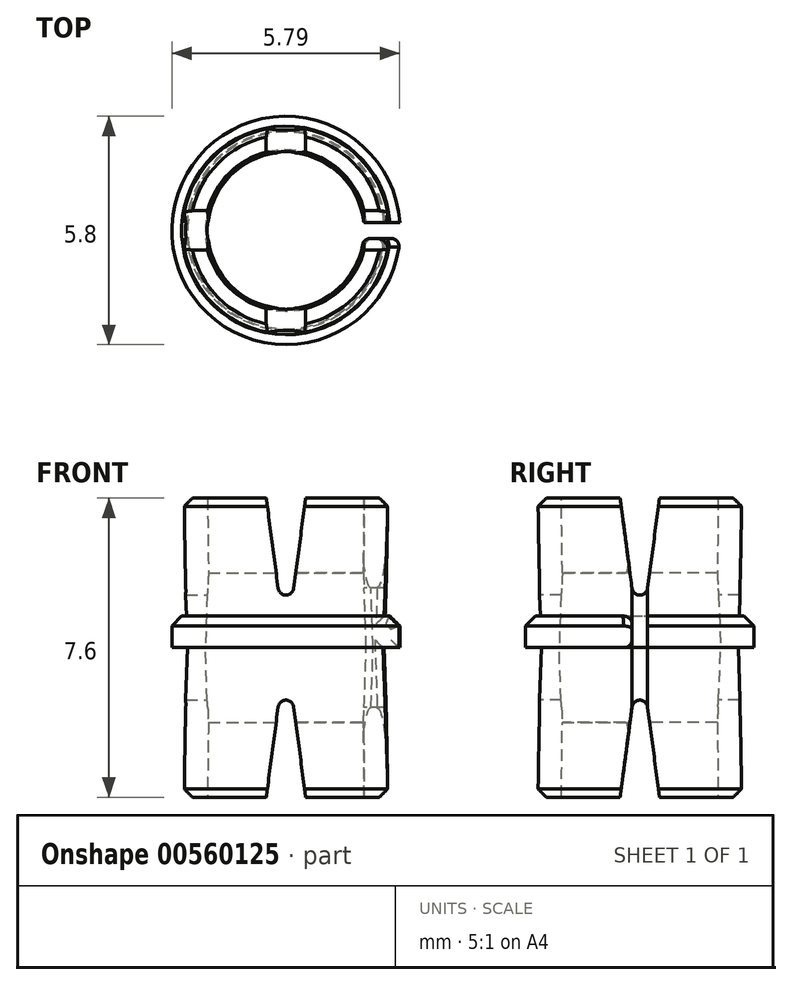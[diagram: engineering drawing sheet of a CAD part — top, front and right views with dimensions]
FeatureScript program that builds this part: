
annotation { "Feature Type Name" : "Feature", "Feature Type Description" : "" }
export const myFeature = defineFeature(function(context is Context, id is Id, definition is map)
    precondition{}
    {
        {
            var Q0;
            Q0=qCreatedBy(makeId("Top.planeOp"),FACE);
            var sketch = newSketch(context, id + "F0", { "sketchPlane" : qUnion([Q0])});
            skCircle(sketch, "E0", {"center": v(0, 0) * mm, "radius": 2.5 * mm});
            skCircle(sketch, "E1", {"center": v(0, 0) * mm, "radius": 2.05 * mm});
            skSolve(sketch);
        }
        {
            var Q0;
            Q0=qSketchRegion(id+"F0",true);
            extrude(context, id + "F1", {"entities" : qUnion([Q0]), "depth" : 3.8 * mm, "offsetDistance" : 25 * mm, "hasDraft" : true, "draftAngle" : 2 * degree, "hasSecondDirection" : true, "secondDirectionOppositeDirection" : true, "secondDirectionDepth" : 3.8 * mm, "hasSecondDirectionDraft" : true, "secondDirectionDraftAngle" : 2 * degree});
        }
        {
            var Q0;
            Q0=qCreatedBy(makeId("Top.planeOp"),FACE);
            var sketch = newSketch(context, id + "F2", { "sketchPlane" : qUnion([Q0])});
            skCircle(sketch, "E2", {"center": v(0, 0) * mm, "radius": 1.92 * mm});
            skSolve(sketch);
        }
        {
            var Q0;
            Q0=qSketchRegion(id+"F2",true);
            extrude(context, id + "F3", {"entities" : qUnion([Q0]), "operationType" : NewBodyOperationType.REMOVE, "endBound" : BoundingType.SYMMETRIC, "oppositeDirection" : true, "depth" : 50 * mm, "offsetDistance" : 25 * mm, "hasDraft" : true, "draftAngle" : 2 * degree});
        }
        {
            var Q0;
            Q0=makeQuery(id+"F1.opExtrude","CAP_EDGE",EDGE,{"disambiguationData":[OSD([sQuery(id+"F0.wireOp",EDGE,"E0")])],"isStart":false});
            var Q1;
            Q1=makeQuery(id+"F1.opExtrude","CAP_EDGE",EDGE,{"disambiguationData":[OSD([sQuery(id+"F0.wireOp",EDGE,"E0")])],"isStart":true});
            chamfer(context, id + "F4", {"entities" : qUnion([Q0, Q1]), "width" : 0.2 * mm, "tangentPropagation" : true});
        }
        {
            var Q0;
            Q0=qCreatedBy(makeId("Right.planeOp"),FACE);
            var sketch = newSketch(context, id + "F5", { "sketchPlane" : qUnion([Q0])});
            skLineSegment(sketch, "E3", {"start": v(0.2, -1.5) * mm, "end": v(0.5, -3.8) * mm});
            skLineSegment(sketch, "E4", {"start": v(0.5, -3.8) * mm, "end": v(-0.5, -3.8) * mm});
            skLineSegment(sketch, "E5", {"start": v(-0.5, -3.8) * mm, "end": v(-0.2, -1.5) * mm});
            skPoint(sketch, "E6.visualSharp", {"position": v(0, 0) * mm});
            skArc(sketch, "E6.filletArc", {"start": v(0.2, -1.5) * mm, "mid": v(0, -1.33) * mm, "end": v(-0.2, -1.5) * mm});
            skArc(sketch, "E7.MirrorCS", {"start": v(0.2, 1.5) * mm, "mid": v(0, 1.33) * mm, "end": v(-0.2, 1.5) * mm});
            skLineSegment(sketch, "E8.MirrorCS", {"start": v(0.2, 1.5) * mm, "end": v(0.5, 3.8) * mm});
            skLineSegment(sketch, "E9.MirrorCS", {"start": v(0.5, 3.8) * mm, "end": v(-0.5, 3.8) * mm});
            skLineSegment(sketch, "E10.MirrorCS", {"start": v(-0.5, 3.8) * mm, "end": v(-0.2, 1.5) * mm});
            skSolve(sketch);
        }
        {
            var Q0;
            Q0=qSketchRegion(id+"F5",true);
            extrude(context, id + "F6", {"entities" : qUnion([Q0]), "operationType" : NewBodyOperationType.REMOVE, "oppositeDirection" : true, "depth" : 25 * mm, "offsetDistance" : 25 * mm, "hasSecondDirection" : true, "secondDirectionOppositeDirection" : false, "secondDirectionDepth" : 25 * mm});
        }
        {
            var Q0;
            Q0=qCreatedBy(makeId("Front.planeOp"),FACE);
            var sketch = newSketch(context, id + "F7", { "sketchPlane" : qUnion([Q0])});
            skLineSegment(sketch, "E11", {"start": v(0.2, -1.5) * mm, "end": v(0.5, -3.8) * mm});
            skLineSegment(sketch, "E12", {"start": v(0.5, -3.8) * mm, "end": v(-0.5, -3.8) * mm});
            skLineSegment(sketch, "E13", {"start": v(-0.5, -3.8) * mm, "end": v(-0.2, -1.5) * mm});
            skPoint(sketch, "E14.visualSharp", {"position": v(0, 0) * mm});
            skArc(sketch, "E14.filletArc", {"start": v(0.2, -1.5) * mm, "mid": v(0, -1.33) * mm, "end": v(-0.2, -1.5) * mm});
            skArc(sketch, "E15.MirrorCS", {"start": v(0.2, 1.5) * mm, "mid": v(0, 1.33) * mm, "end": v(-0.2, 1.5) * mm});
            skLineSegment(sketch, "E16.MirrorCS", {"start": v(0.2, 1.5) * mm, "end": v(0.5, 3.8) * mm});
            skLineSegment(sketch, "E17.MirrorCS", {"start": v(0.5, 3.8) * mm, "end": v(-0.5, 3.8) * mm});
            skLineSegment(sketch, "E18.MirrorCS", {"start": v(-0.5, 3.8) * mm, "end": v(-0.2, 1.5) * mm});
            skSolve(sketch);
        }
        {
            var Q0;
            Q0=qSketchRegion(id+"F7",true);
            extrude(context, id + "F8", {"entities" : qUnion([Q0]), "operationType" : NewBodyOperationType.REMOVE, "oppositeDirection" : true, "depth" : 25 * mm, "offsetDistance" : 25 * mm, "hasSecondDirection" : true, "secondDirectionOppositeDirection" : false, "secondDirectionDepth" : 25 * mm});
        }
        {
            var Q0;
            Q0=qCreatedBy(makeId("Front.planeOp"),FACE);
            var sketch = newSketch(context, id + "F9", { "sketchPlane" : qUnion([Q0])});
            skLineSegment(sketch, "E19.bottom", {"start": v(2.4, 0.8) * mm, "end": v(2.9, 0.8) * mm});
            skLineSegment(sketch, "E19.top", {"start": v(2.4, 0) * mm, "end": v(2.9, 0) * mm});
            skLineSegment(sketch, "E19.left", {"start": v(2.4, 0.8) * mm, "end": v(2.4, 0) * mm});
            skLineSegment(sketch, "E19.right", {"start": v(2.9, 0.8) * mm, "end": v(2.9, 0) * mm});
            skLineSegment(sketch, "E20", {"start": v(0, 0) * mm, "end": v(0, 15.44) * mm, "construction": true});
            skSolve(sketch);
        }
        {
            var Q0;
            Q0=makeQuery(id+"F9.imprint","IMPRINT",FACE,{"disambiguationData":[TD([[makeQuery(id+"F9.imprint","IMPRINT",EDGE,{"derivedFrom":sQuery(id+"F9.wireOp",EDGE,"E19.bottom")}),-1.0]])]});
            var Q1;
            Q1=sQuery(id+"F9.wireOp",EDGE,"E20");
            var Q2;
            Q2=sQuery(id+"F9.wireOp",EDGE,"E20");
            revolve(context, id + "F10", {"operationType" : NewBodyOperationType.ADD, "entities" : qUnion([Q0]), "surfaceEntities" : qUnion([Q1]), "axis" : qUnion([Q2]), "revolveType" : RevolveType.FULL});
        }
        {
            var Q0;
            Q0=makeQuery(id+"F10.opRevolve","SWEPT_EDGE",EDGE,{"disambiguationData":[OSD([sQuery(id+"F9.wireOp",EDGE,"E19.bottom"),sQuery(id+"F9.wireOp",EDGE,"E19.right")])]});
            chamfer(context, id + "F11", {"entities" : qUnion([Q0]), "width" : 0.25 * mm, "tangentPropagation" : true});
        }
        {
            var Q0;
            Q0=qCreatedBy(makeId("Top.planeOp"),FACE);
            var sketch = newSketch(context, id + "F12", { "sketchPlane" : qUnion([Q0])});
            skLineSegment(sketch, "E21", {"start": v(5.06, -0.2) * mm, "end": v(0, -0.2) * mm});
            skLineSegment(sketch, "E22", {"start": v(5.06, 0.2) * mm, "end": v(0, 0.2) * mm});
            skLineSegment(sketch, "E23", {"start": v(0, 0.2) * mm, "end": v(0, -0.2) * mm});
            skLineSegment(sketch, "E24", {"start": v(5.06, 0.2) * mm, "end": v(5.06, -0.2) * mm});
            skSolve(sketch);
        }
        {
            var Q0;
            Q0=makeQuery(id+"F12.imprint","IMPRINT",FACE,{"disambiguationData":[TD([[makeQuery(id+"F12.imprint","IMPRINT",EDGE,{"derivedFrom":sQuery(id+"F12.wireOp",EDGE,"E21")}),-1.0]])]});
            extrude(context, id + "F13", {"entities" : qUnion([Q0]), "operationType" : NewBodyOperationType.REMOVE, "depth" : 25 * mm, "offsetDistance" : 25 * mm, "hasSecondDirection" : true, "secondDirectionOppositeDirection" : true, "secondDirectionDepth" : 25 * mm});
        }
        {
            var Q0;
            Q0=makeQuery(id+"F13.boolean.opBoolean","INTERSECT",EDGE,{"derivedFrom":[makeQuery(id+"F1.*.split.splitOp","SPLIT",FACE,{"derivedFrom":makeQuery(id+"F1.opExtrude","SWEPT_FACE",FACE,{"disambiguationData":[OSD([sQuery(id+"F0.wireOp",EDGE,"E1")])]})}),makeQuery(id+"F13.opExtrude","SWEPT_FACE",FACE,{"disambiguationData":[OSD([sQuery(id+"F12.wireOp",EDGE,"yXu5fMNr-nfGE-pTTA-gAb4-QGezEtGPO8pn")])]})]});
            var Q1;
            Q1=makeQuery(id+"F13.boolean.opBoolean","INTERSECT",EDGE,{"derivedFrom":[makeQuery(id+"F1.*.split.splitOp","SPLIT",FACE,{"derivedFrom":makeQuery(id+"F1.opExtrude","SWEPT_FACE",FACE,{"disambiguationData":[OSD([sQuery(id+"F0.wireOp",EDGE,"E1")])]}),"isFromBackBody":true}),makeQuery(id+"F13.opExtrude","SWEPT_FACE",FACE,{"disambiguationData":[OSD([sQuery(id+"F12.wireOp",EDGE,"yXu5fMNr-nfGE-pTTA-gAb4-QGezEtGPO8pn")])]})]});
            var Q2;
            Q2=makeQuery(id+"F13.boolean.opBoolean","INTERSECT",EDGE,{"derivedFrom":[makeQuery(id+"F1.*.split.splitOp","SPLIT",FACE,{"derivedFrom":makeQuery(id+"F1.opExtrude","SWEPT_FACE",FACE,{"disambiguationData":[OSD([sQuery(id+"F0.wireOp",EDGE,"E1")])]}),"isFromBackBody":true}),makeQuery(id+"F13.opExtrude","SWEPT_FACE",FACE,{"disambiguationData":[OSD([sQuery(id+"F12.wireOp",EDGE,"E21")])]})]});
            var Q3;
            Q3=makeQuery(id+"F13.boolean.opBoolean","INTERSECT",EDGE,{"derivedFrom":[makeQuery(id+"F1.*.split.splitOp","SPLIT",FACE,{"derivedFrom":makeQuery(id+"F1.opExtrude","SWEPT_FACE",FACE,{"disambiguationData":[OSD([sQuery(id+"F0.wireOp",EDGE,"E1")])]})}),makeQuery(id+"F13.opExtrude","SWEPT_FACE",FACE,{"disambiguationData":[OSD([sQuery(id+"F12.wireOp",EDGE,"E21")])]})]});
            var Q4;
            Q4=makeQuery(id+"F13.boolean.opBoolean","INTERSECT",EDGE,{"derivedFrom":[makeQuery(id+"F1.*.split.splitOp","SPLIT",FACE,{"derivedFrom":makeQuery(id+"F1.opExtrude","SWEPT_FACE",FACE,{"disambiguationData":[OSD([sQuery(id+"F0.wireOp",EDGE,"E0")])]}),"isFromBackBody":true}),makeQuery(id+"F13.opExtrude","SWEPT_FACE",FACE,{"disambiguationData":[OSD([sQuery(id+"F12.wireOp",EDGE,"E21")])]})]});
            var Q5;
            Q5=makeQuery(id+"F13.boolean.opBoolean","INTERSECT",EDGE,{"derivedFrom":[makeQuery(id+"F1.*.split.splitOp","SPLIT",FACE,{"derivedFrom":makeQuery(id+"F1.opExtrude","SWEPT_FACE",FACE,{"disambiguationData":[OSD([sQuery(id+"F0.wireOp",EDGE,"E0")])]})}),makeQuery(id+"F13.opExtrude","SWEPT_FACE",FACE,{"disambiguationData":[OSD([sQuery(id+"F12.wireOp",EDGE,"E21")])]})]});
            var Q6;
            Q6=makeQuery(id+"F13.boolean.opBoolean","INTERSECT",EDGE,{"derivedFrom":[makeQuery(id+"F1.*.split.splitOp","SPLIT",FACE,{"derivedFrom":makeQuery(id+"F1.opExtrude","SWEPT_FACE",FACE,{"disambiguationData":[OSD([sQuery(id+"F0.wireOp",EDGE,"E0")])]})}),makeQuery(id+"F13.opExtrude","SWEPT_FACE",FACE,{"disambiguationData":[OSD([sQuery(id+"F12.wireOp",EDGE,"yXu5fMNr-nfGE-pTTA-gAb4-QGezEtGPO8pn")])]})]});
            var Q7;
            Q7=makeQuery(id+"F13.boolean.opBoolean","INTERSECT",EDGE,{"derivedFrom":[makeQuery(id+"F1.*.split.splitOp","SPLIT",FACE,{"derivedFrom":makeQuery(id+"F1.opExtrude","SWEPT_FACE",FACE,{"disambiguationData":[OSD([sQuery(id+"F0.wireOp",EDGE,"E0")])]}),"isFromBackBody":true}),makeQuery(id+"F13.opExtrude","SWEPT_FACE",FACE,{"disambiguationData":[OSD([sQuery(id+"F12.wireOp",EDGE,"yXu5fMNr-nfGE-pTTA-gAb4-QGezEtGPO8pn")])]})]});
            fillet(context, id + "F14", {"entities" : qUnion([Q0, Q1, Q2, Q3, Q4, Q5, Q6, Q7]), "radius" : 0.2 * mm, "tangentPropagation" : true, "allowEdgeOverflow" : false});
        }
        {
            var Q0;
            Q0=makeQuery(id+"F13.boolean.opBoolean","INTERSECT",EDGE,{"derivedFrom":[makeQuery(id+"F10.opRevolve","SWEPT_FACE",FACE,{"disambiguationData":[OSD([sQuery(id+"F9.wireOp",EDGE,"E19.top")])]}),makeQuery(id+"F13.opExtrude","SWEPT_FACE",FACE,{"disambiguationData":[OSD([sQuery(id+"F12.wireOp",EDGE,"E21")])]})]});
            var Q1;
            Q1=makeQuery(id+"F13.boolean.opBoolean","INTERSECT",EDGE,{"derivedFrom":[makeQuery(id+"F10.opRevolve","SWEPT_FACE",FACE,{"disambiguationData":[OSD([sQuery(id+"F9.wireOp",EDGE,"E19.right")])]}),makeQuery(id+"F13.opExtrude","SWEPT_FACE",FACE,{"disambiguationData":[OSD([sQuery(id+"F12.wireOp",EDGE,"E21")])]})]});
            var Q2;
            Q2=makeQuery(id+"F13.boolean.opBoolean","INTERSECT",EDGE,{"derivedFrom":[makeQuery(id+"F11.opChamfer","BLEND_FACE",FACE,{"disambiguationData":[OSD([sQuery(id+"F9.wireOp",EDGE,"E19.bottom"),sQuery(id+"F9.wireOp",EDGE,"E19.right")])]}),makeQuery(id+"F13.opExtrude","SWEPT_FACE",FACE,{"disambiguationData":[OSD([sQuery(id+"F12.wireOp",EDGE,"E21")])]})]});
            var Q3;
            Q3=makeQuery(id+"F13.boolean.opBoolean","INTERSECT",EDGE,{"derivedFrom":[makeQuery(id+"F10.opRevolve","SWEPT_FACE",FACE,{"disambiguationData":[OSD([sQuery(id+"F9.wireOp",EDGE,"E19.bottom")])]}),makeQuery(id+"F13.opExtrude","SWEPT_FACE",FACE,{"disambiguationData":[OSD([sQuery(id+"F12.wireOp",EDGE,"E21")])]})]});
            var Q4;
            Q4=makeQuery(id+"F13.boolean.opBoolean","INTERSECT",EDGE,{"derivedFrom":[makeQuery(id+"F10.opRevolve","SWEPT_FACE",FACE,{"disambiguationData":[OSD([sQuery(id+"F9.wireOp",EDGE,"E19.top")])]}),makeQuery(id+"F13.opExtrude","SWEPT_FACE",FACE,{"disambiguationData":[OSD([sQuery(id+"F12.wireOp",EDGE,"yXu5fMNr-nfGE-pTTA-gAb4-QGezEtGPO8pn")])]})]});
            var Q5;
            Q5=makeQuery(id+"F13.boolean.opBoolean","INTERSECT",EDGE,{"derivedFrom":[makeQuery(id+"F10.opRevolve","SWEPT_FACE",FACE,{"disambiguationData":[OSD([sQuery(id+"F9.wireOp",EDGE,"E19.right")])]}),makeQuery(id+"F13.opExtrude","SWEPT_FACE",FACE,{"disambiguationData":[OSD([sQuery(id+"F12.wireOp",EDGE,"yXu5fMNr-nfGE-pTTA-gAb4-QGezEtGPO8pn")])]})]});
            var Q6;
            Q6=makeQuery(id+"F13.boolean.opBoolean","INTERSECT",EDGE,{"derivedFrom":[makeQuery(id+"F11.opChamfer","BLEND_FACE",FACE,{"disambiguationData":[OSD([sQuery(id+"F9.wireOp",EDGE,"E19.bottom"),sQuery(id+"F9.wireOp",EDGE,"E19.right")])]}),makeQuery(id+"F13.opExtrude","SWEPT_FACE",FACE,{"disambiguationData":[OSD([sQuery(id+"F12.wireOp",EDGE,"yXu5fMNr-nfGE-pTTA-gAb4-QGezEtGPO8pn")])]})]});
            var Q7;
            Q7=makeQuery(id+"F13.boolean.opBoolean","INTERSECT",EDGE,{"derivedFrom":[makeQuery(id+"F10.opRevolve","SWEPT_FACE",FACE,{"disambiguationData":[OSD([sQuery(id+"F9.wireOp",EDGE,"E19.bottom")])]}),makeQuery(id+"F13.opExtrude","SWEPT_FACE",FACE,{"disambiguationData":[OSD([sQuery(id+"F12.wireOp",EDGE,"yXu5fMNr-nfGE-pTTA-gAb4-QGezEtGPO8pn")])]})]});
            fillet(context, id + "F15", {"entities" : qUnion([Q0, Q1, Q2, Q3, Q4, Q5, Q6, Q7]), "radius" : 0.2 * mm, "tangentPropagation" : true, "allowEdgeOverflow" : false});
        }
    });
